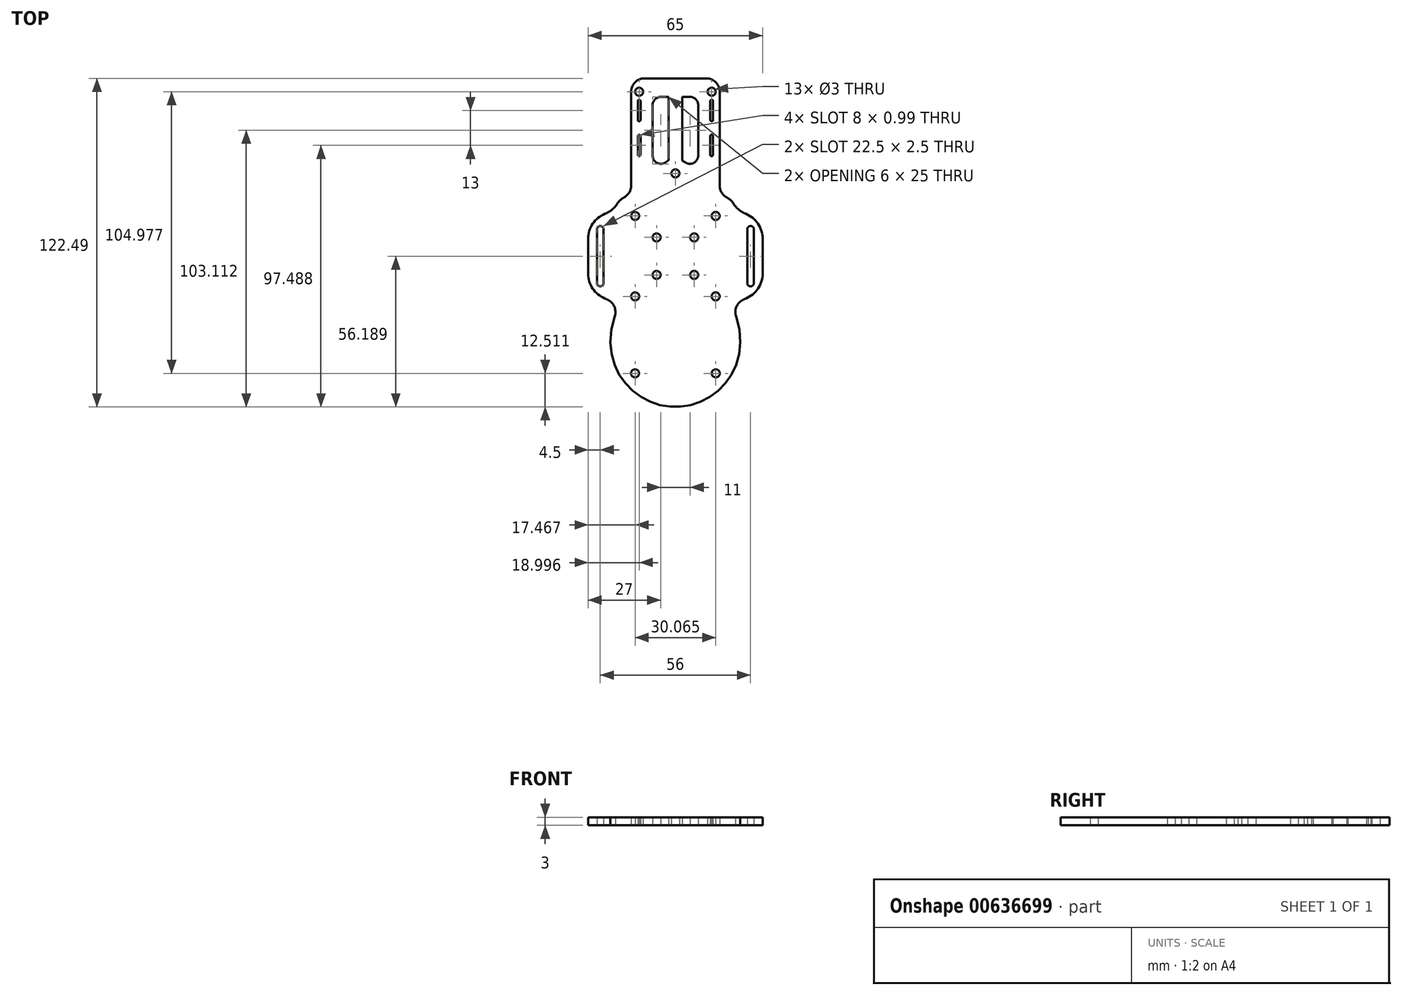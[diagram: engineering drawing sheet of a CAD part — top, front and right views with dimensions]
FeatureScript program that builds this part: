
annotation { "Feature Type Name" : "Feature", "Feature Type Description" : "" }
export const myFeature = defineFeature(function(context is Context, id is Id, definition is map)
    precondition{}
    {
        {
            var Q0;
            Q0=qCreatedBy(makeId("Top.planeOp"),FACE);
            var sketch = newSketch(context, id + "F0", { "sketchPlane" : qUnion([Q0])});
            skPoint(sketch, "E0.middle", {"position": v(3.13, -5.79) * mm});
            skPoint(sketch, "E1.middle", {"position": v(0, 0) * mm});
            skCircle(sketch, "E2", {"center": v(15, 15) * mm, "radius": 1.5 * mm});
            skCircle(sketch, "E3", {"center": v(-15, 15) * mm, "radius": 1.5 * mm});
            skCircle(sketch, "E4", {"center": v(-15, -15) * mm, "radius": 1.5 * mm});
            skPoint(sketch, "E5.visualSharp", {"position": v(-22.5, -22.5) * mm});
            skCircle(sketch, "E6.MirrorC", {"center": v(7, -7) * mm, "radius": 1.5 * mm});
            skCircle(sketch, "E7.MirrorC", {"center": v(-7, -7) * mm, "radius": 1.5 * mm});
            skCircle(sketch, "E8.MirrorC", {"center": v(-7, 7) * mm, "radius": 1.5 * mm});
            skCircle(sketch, "E9.MirrorC", {"center": v(7, 7) * mm, "radius": 1.5 * mm});
            skPoint(sketch, "E10.visualSharp", {"position": v(-22.5, 22.5) * mm});
            skArc(sketch, "E10.filletArc", {"start": v(-19.23, 21.84) * mm, "mid": v(-20.55, 20.93) * mm, "end": v(-21.58, 19.7) * mm});
            skPoint(sketch, "E11.visualSharp", {"position": v(22.5, 22.5) * mm});
            skArc(sketch, "E11.filletArc", {"start": v(21.58, 19.7) * mm, "mid": v(20.55, 20.93) * mm, "end": v(19.23, 21.84) * mm});
            skPoint(sketch, "E12.visualSharp", {"position": v(22.5, -22.5) * mm});
            skCircle(sketch, "E13.MirrorC", {"center": v(15, -15) * mm, "radius": 1.5 * mm});
            skLineSegment(sketch, "E14", {"start": v(22.5, 16.5) * mm, "end": v(22.5, 16.5) * mm});
            skLineSegment(sketch, "E15", {"start": v(22.5, -16.5) * mm, "end": v(22.5, -16.5) * mm});
            skLineSegment(sketch, "E16", {"start": v(32.5, -6.5) * mm, "end": v(32.5, 6.5) * mm});
            skPoint(sketch, "E17.visualSharp", {"position": v(32.5, 16.5) * mm});
            skArc(sketch, "E17.filletArc", {"start": v(32.5, 6.5) * mm, "mid": v(30.8, 12.08) * mm, "end": v(26.27, 15.76) * mm});
            skPoint(sketch, "E18.visualSharp", {"position": v(32.5, -16.5) * mm});
            skArc(sketch, "E18.filletArc", {"start": v(26.27, -15.76) * mm, "mid": v(30.8, -12.08) * mm, "end": v(32.5, -6.5) * mm});
            skPoint(sketch, "E19.visualSharp", {"position": v(22.5, -16.5) * mm});
            skArc(sketch, "E19.filletArc", {"start": v(26.27, -15.76) * mm, "mid": v(25.43, -16.15) * mm, "end": v(24.63, -16.62) * mm});
            skPoint(sketch, "E20.visualSharp", {"position": v(22.5, 16.5) * mm});
            skArc(sketch, "E20.filletArc", {"start": v(21.58, 19.7) * mm, "mid": v(23.62, 17.36) * mm, "end": v(26.27, 15.76) * mm});
            skLineSegment(sketch, "E21", {"start": v(-22.5, 16.5) * mm, "end": v(-22.5, 16.5) * mm});
            skLineSegment(sketch, "E22", {"start": v(-22.5, -16.5) * mm, "end": v(-22.5, -16.5) * mm});
            skLineSegment(sketch, "E23", {"start": v(-32.5, -6.5) * mm, "end": v(-32.5, 6.5) * mm});
            skPoint(sketch, "E24.visualSharp", {"position": v(-32.5, 16.5) * mm});
            skArc(sketch, "E24.filletArc", {"start": v(-26.27, 15.76) * mm, "mid": v(-30.8, 12.08) * mm, "end": v(-32.5, 6.5) * mm});
            skPoint(sketch, "E25.visualSharp", {"position": v(-32.5, -16.5) * mm});
            skArc(sketch, "E25.filletArc", {"start": v(-32.5, -6.5) * mm, "mid": v(-30.8, -12.08) * mm, "end": v(-26.27, -15.76) * mm});
            skPoint(sketch, "E26.visualSharp", {"position": v(-22.5, 16.5) * mm});
            skArc(sketch, "E26.filletArc", {"start": v(-26.27, 15.76) * mm, "mid": v(-23.62, 17.36) * mm, "end": v(-21.58, 19.7) * mm});
            skPoint(sketch, "E27.visualSharp", {"position": v(-22.5, -16.5) * mm});
            skArc(sketch, "E27.filletArc", {"start": v(-24.63, -16.62) * mm, "mid": v(-25.43, -16.15) * mm, "end": v(-26.27, -15.76) * mm});
            skArc(sketch, "E28", {"start": v(29.24, 9.88) * mm, "mid": v(28.06, 11.25) * mm, "end": v(26.75, 10) * mm});
            skArc(sketch, "E29", {"start": v(26.75, -10) * mm, "mid": v(28, -11.25) * mm, "end": v(29.25, -10) * mm});
            skLineSegment(sketch, "E30", {"start": v(26.75, 10) * mm, "end": v(26.75, -10) * mm});
            skLineSegment(sketch, "E31", {"start": v(29.24, 10.12) * mm, "end": v(29.25, -10) * mm});
            skLineSegment(sketch, "E32.MirrorCS", {"start": v(-26.75, 10) * mm, "end": v(-26.75, -10) * mm});
            skLineSegment(sketch, "E33.MirrorCS", {"start": v(-29.24, 10.12) * mm, "end": v(-29.25, -10) * mm});
            skArc(sketch, "E34.MirrorCS", {"start": v(-29.24, 9.88) * mm, "mid": v(-28.06, 11.25) * mm, "end": v(-26.75, 10) * mm});
            skArc(sketch, "E35.MirrorCS", {"start": v(-26.75, -10) * mm, "mid": v(-28, -11.25) * mm, "end": v(-29.25, -10) * mm});
            skLineSegment(sketch, "E36", {"start": v(-16.5, 26.3) * mm, "end": v(-16.5, 61.3) * mm});
            skLineSegment(sketch, "E37", {"start": v(16.5, 26.3) * mm, "end": v(16.5, 61.3) * mm});
            skLineSegment(sketch, "E38", {"start": v(11.5, 66.3) * mm, "end": v(-11.5, 66.3) * mm});
            skPoint(sketch, "E39.visualSharp", {"position": v(-16.5, 22.5) * mm});
            skArc(sketch, "E39.filletArc", {"start": v(-19.23, 21.84) * mm, "mid": v(-17.24, 23.69) * mm, "end": v(-16.5, 26.3) * mm});
            skPoint(sketch, "E40.visualSharp", {"position": v(16.5, 22.5) * mm});
            skArc(sketch, "E40.filletArc", {"start": v(16.5, 26.3) * mm, "mid": v(17.24, 23.69) * mm, "end": v(19.23, 21.84) * mm});
            skPoint(sketch, "E41.visualSharp", {"position": v(-16.5, 66.3) * mm});
            skArc(sketch, "E41.filletArc", {"start": v(-11.5, 66.3) * mm, "mid": v(-15.04, 64.83) * mm, "end": v(-16.5, 61.3) * mm});
            skPoint(sketch, "E42.visualSharp", {"position": v(16.5, 66.3) * mm});
            skArc(sketch, "E42.filletArc", {"start": v(16.5, 61.3) * mm, "mid": v(15.04, 64.83) * mm, "end": v(11.5, 66.3) * mm});
            skLineSegment(sketch, "E43", {"start": v(-8.5, 56.3) * mm, "end": v(-8.5, 37.54) * mm});
            skLineSegment(sketch, "E44", {"start": v(-3.64, 34.95) * mm, "end": v(-2.5, 35.71) * mm});
            skLineSegment(sketch, "E45", {"start": v(-2.5, 35.71) * mm, "end": v(-2.5, 59.42) * mm});
            skLineSegment(sketch, "E46", {"start": v(-2.5, 59.42) * mm, "end": v(-5.38, 59.42) * mm});
            skLineSegment(sketch, "E47.MirrorCS", {"start": v(2.5, 35.98) * mm, "end": v(2.5, 59.42) * mm});
            skLineSegment(sketch, "E48.MirrorCS", {"start": v(8.5, 56.3) * mm, "end": v(8.5, 37.54) * mm});
            skLineSegment(sketch, "E49.MirrorCS", {"start": v(3.64, 34.95) * mm, "end": v(2.73, 35.56) * mm});
            skLineSegment(sketch, "E50.MirrorCS", {"start": v(2.5, 59.42) * mm, "end": v(5.38, 59.42) * mm});
            skArc(sketch, "E51", {"start": v(14, 57.8) * mm, "mid": v(13.46, 58.3) * mm, "end": v(13, 57.71) * mm});
            skArc(sketch, "E52", {"start": v(13, 37.88) * mm, "mid": v(13.46, 37.3) * mm, "end": v(14, 37.8) * mm});
            skLineSegment(sketch, "E53", {"start": v(14, 57.8) * mm, "end": v(14, 50.8) * mm});
            skLineSegment(sketch, "E54", {"start": v(13, 57.88) * mm, "end": v(13, 50.71) * mm});
            skArc(sketch, "E55.MirrorCS", {"start": v(-14, 57.8) * mm, "mid": v(-13.46, 58.3) * mm, "end": v(-13, 57.71) * mm});
            skArc(sketch, "E56.MirrorCS", {"start": v(-13, 37.88) * mm, "mid": v(-13.46, 37.3) * mm, "end": v(-14, 37.8) * mm});
            skLineSegment(sketch, "E57.MirrorCS", {"start": v(-13, 57.88) * mm, "end": v(-13, 50.71) * mm});
            skLineSegment(sketch, "E58.MirrorCS", {"start": v(-14, 57.8) * mm, "end": v(-14, 50.8) * mm});
            skPoint(sketch, "E59.visualSharp", {"position": v(-8.5, 31.7) * mm});
            skArc(sketch, "E59.filletArc", {"start": v(-8.5, 37.54) * mm, "mid": v(-6.85, 34.79) * mm, "end": v(-3.64, 34.95) * mm});
            skPoint(sketch, "E60.visualSharp", {"position": v(-8.5, 59.42) * mm});
            skArc(sketch, "E60.filletArc", {"start": v(-5.38, 59.42) * mm, "mid": v(-7.59, 58.5) * mm, "end": v(-8.5, 56.3) * mm});
            skPoint(sketch, "E61.visualSharp", {"position": v(8.5, 59.42) * mm});
            skArc(sketch, "E61.filletArc", {"start": v(8.5, 56.3) * mm, "mid": v(7.59, 58.5) * mm, "end": v(5.38, 59.42) * mm});
            skPoint(sketch, "E62.visualSharp", {"position": v(8.5, 31.7) * mm});
            skArc(sketch, "E62.filletArc", {"start": v(3.64, 34.95) * mm, "mid": v(6.85, 34.79) * mm, "end": v(8.5, 37.54) * mm});
            skPoint(sketch, "E63.visualSharp", {"position": v(2.5, 35.71) * mm});
            skArc(sketch, "E63.filletArc", {"start": v(2.5, 35.98) * mm, "mid": v(2.56, 35.74) * mm, "end": v(2.73, 35.56) * mm});
            skCircle(sketch, "E64", {"center": v(-13.5, 61.3) * mm, "radius": 1.5 * mm});
            skCircle(sketch, "E65.MirrorC", {"center": v(13.5, 61.3) * mm, "radius": 1.5 * mm});
            skArc(sketch, "E66", {"start": v(13, 50.88) * mm, "mid": v(13.46, 50.3) * mm, "end": v(14, 50.8) * mm});
            skArc(sketch, "E67", {"start": v(14, 44.8) * mm, "mid": v(13.46, 45.3) * mm, "end": v(13, 44.71) * mm});
            skArc(sketch, "E68.MirrorC", {"start": v(-13, 50.88) * mm, "mid": v(-13.46, 50.3) * mm, "end": v(-14, 50.8) * mm});
            skArc(sketch, "E69.MirrorC", {"start": v(-14, 44.8) * mm, "mid": v(-13.46, 45.3) * mm, "end": v(-13, 44.71) * mm});
            skLineSegment(sketch, "E70.trimOffspring", {"start": v(13, 44.88) * mm, "end": v(13, 37.71) * mm});
            skLineSegment(sketch, "E71.trimOffspring", {"start": v(14, 44.8) * mm, "end": v(14, 37.8) * mm});
            skLineSegment(sketch, "E72.trimOffspring", {"start": v(-13, 44.88) * mm, "end": v(-13, 37.71) * mm});
            skLineSegment(sketch, "E73.trimOffspring", {"start": v(-14, 44.8) * mm, "end": v(-14, 37.8) * mm});
            skPoint(sketch, "E74.center.orphan", {"position": v(0, -22.5) * mm});
            skFitSpline(sketch, "E75", {"points": [v(-21.58, -19.7) * mm, v(0, -56.19) * mm, v(21.58, -19.7) * mm], "startDerivative": vector(-53.16, -127.04) * mm, "endDerivative": vector(-53.16, 127.04) * mm});
            skFitSpline(sketch, "E76.0", {"points": [v(-12.35, -23.56) * mm, v(-13.18, -25.53) * mm, v(-14.18, -29.14) * mm, v(-14.29, -33.52) * mm, v(-13.43, -37.12) * mm, v(-11.78, -40.17) * mm, v(-9.43, -42.74) * mm, v(-7, -44.37) * mm, v(-4.89, -45.3) * mm, v(-3.25, -45.82) * mm, v(-1.89, -46.07) * mm, v(-0.8, -46.17) * mm, v(0, -46.2) * mm, v(0.8, -46.17) * mm, v(1.89, -46.07) * mm, v(3.25, -45.82) * mm, v(4.89, -45.3) * mm, v(7, -44.37) * mm, v(9.43, -42.74) * mm, v(11.78, -40.17) * mm, v(13.43, -37.12) * mm, v(14.29, -33.52) * mm, v(14.18, -29.14) * mm, v(13.18, -25.53) * mm, v(12.35, -23.56) * mm]});
            skArc(sketch, "E77.filletArc", {"start": v(24.63, -16.62) * mm, "mid": v(22.62, -19.15) * mm, "end": v(22.59, -22.4) * mm});
            skArc(sketch, "E78.filletArc", {"start": v(-22.59, -22.4) * mm, "mid": v(-22.62, -19.15) * mm, "end": v(-24.63, -16.62) * mm});
            skArc(sketch, "E79", {"start": v(10.1, -22.66) * mm, "mid": v(0, -20.92) * mm, "end": v(-10.1, -22.66) * mm});
            skPoint(sketch, "E80.visualSharp", {"position": v(-12.35, -23.56) * mm});
            skArc(sketch, "E80.filletArc", {"start": v(-10.1, -22.66) * mm, "mid": v(-12.03, -23.9) * mm, "end": v(-13.2, -25.86) * mm});
            skPoint(sketch, "E81.visualSharp", {"position": v(12.35, -23.56) * mm});
            skArc(sketch, "E81.filletArc", {"start": v(13.2, -25.86) * mm, "mid": v(12.03, -23.9) * mm, "end": v(10.1, -22.66) * mm});
            skCircle(sketch, "E82", {"center": v(0, 30.87) * mm, "radius": 1.5 * mm});
            skCircle(sketch, "E83", {"center": v(15.03, -43.68) * mm, "radius": 1.5 * mm});
            skCircle(sketch, "E84.MirrorC", {"center": v(-15.03, -43.68) * mm, "radius": 1.5 * mm});
            skSolve(sketch);
        }
        {
            var Q0;
            Q0=makeQuery(id+"F0.imprint","IMPRINT",FACE,{"disambiguationData":[TD([[makeQuery(id+"F0.imprint","IMPRINT",EDGE,{"derivedFrom":sQuery(id+"F0.wireOp",EDGE,"ee04861f-8e55-4c6a-9696-76f970dc2b79")}),-1.0]])]});
            var Q1;
            Q1=makeQuery(id+"F0.imprint","IMPRINT",FACE,{"disambiguationData":[TD([[makeQuery(id+"F0.imprint","IMPRINT",EDGE,{"derivedFrom":sQuery(id+"F0.wireOp",EDGE,"938f7499-d4fb-4266-8f5c-ac350d31f9f6")}),-1.0]])]});
            var Q2;
            Q2=makeQuery(id+"F0.imprint","IMPRINT",FACE,{"disambiguationData":[TD([[makeQuery(id+"F0.imprint","IMPRINT",EDGE,{"derivedFrom":sQuery(id+"F0.wireOp",EDGE,"E2")}),-1.0]])]});
            extrude(context, id + "F1", {"entities" : qUnion([Q0, Q1, Q2]), "depth" : 3 * mm, "offsetDistance" : 25 * mm});
        }
    });
